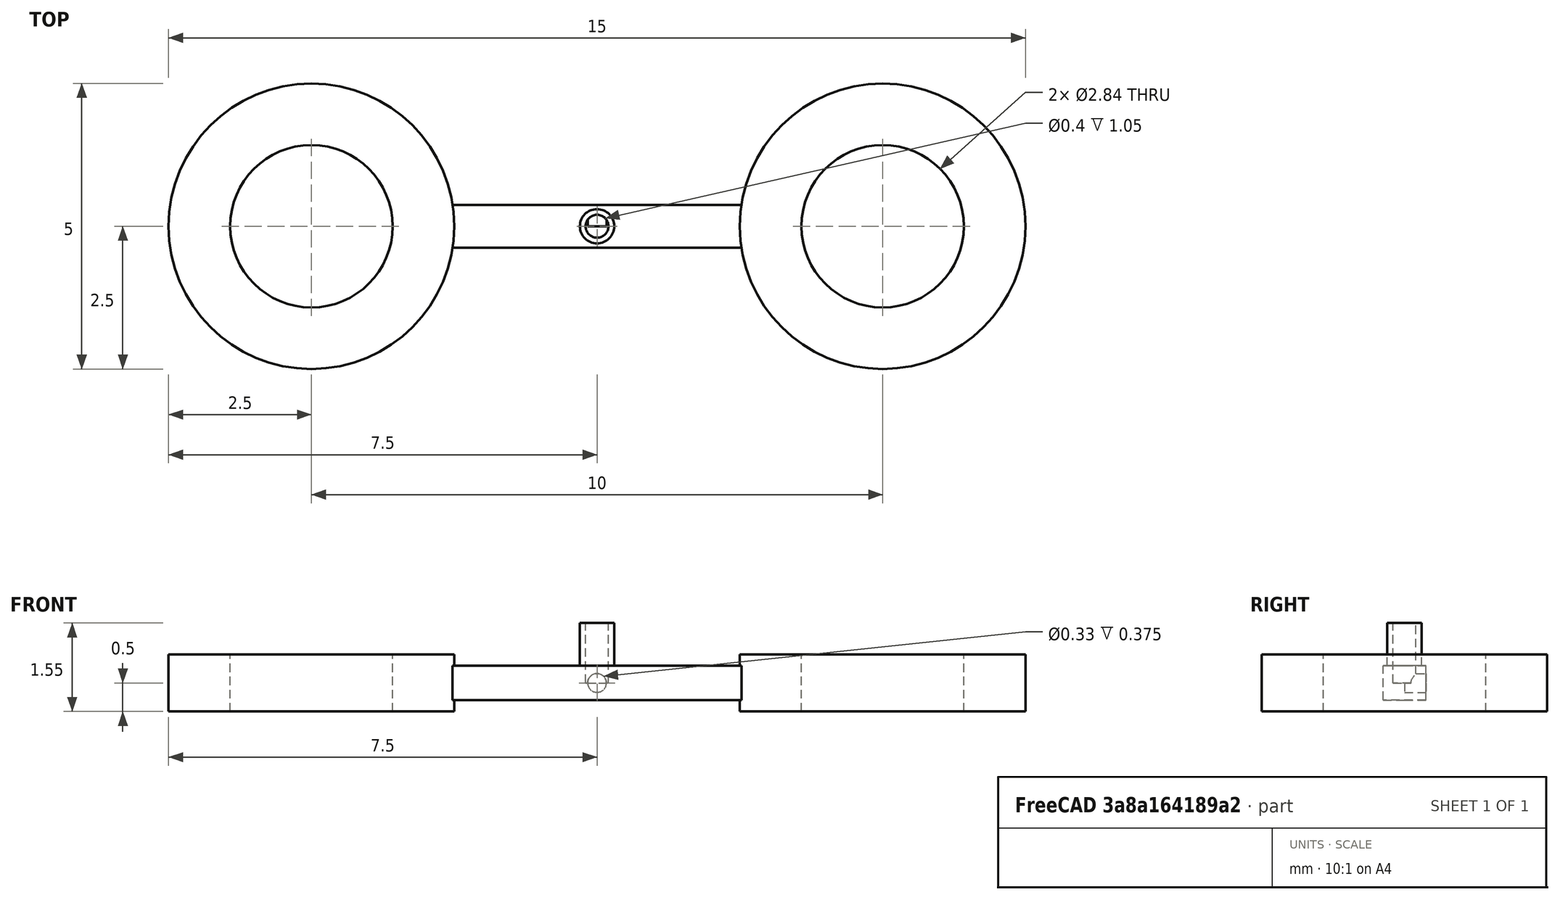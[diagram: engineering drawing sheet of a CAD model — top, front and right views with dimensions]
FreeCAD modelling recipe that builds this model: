
FCSTD DOCUMENT  (FreeCAD 0.18R15536 (Git))
Label: bowtie_3
License: All rights reserved
LicenseURL: http://en.wikipedia.org/wiki/All_rights_reserved
objects: Part::Cylinder×7, Part::MultiFuse×2, Part::Box×1, Spreadsheet::Sheet×1, Part::Cut×1
note: 11 computed .brp shape members not serialized (recipe doc carries the construction recipe); baked Part::Feature solids carry a one-line shape summary decoded from their .brp

FEATURE [Part::Cylinder] Cylinder138  label="BowTieInjectorWire"
  Angle = 360
  AttacherType = Attacher::AttachEngine3D
  Height = 8
  Placement = pos=(0,0,0) rot=(-1,0,0;1.5708rad)
  Radius = 0.165
  expr: Radius = 0.33000000000000002 / 2
FEATURE [Part::Cylinder] Cylinder136  label="BowTieNozzle"
  Angle = 360
  AttacherType = Attacher::AttachEngine3D
  Height = 9
  Radius = 0.2
FEATURE [Part::Cylinder] Cylinder  label="MountingHole1"
  Angle = 360
  AttacherType = Attacher::AttachEngine3D
  Height = 2
  Placement = pos=(-5,0,-1) rot=(0,0,1;0rad)
  Radius = 1.422
  expr: Placement.Base.x = -Sizes.STRIP_LENGTH / 2
  expr: Radius = Sizes.MOUNTING_ID / 2
FEATURE [Part::Box] Box  label="Strip"
  AttacherType = Attacher::AttachEngine3D
  Height = 0.6
  Length = 10
  Placement = pos=(-5,-0.375,-0.3) rot=(0,0,1;0rad)
  Width = 0.75
  expr: Width = Sizes.STRIP_WIDTH
  expr: Placement.Base.y = -Sizes.STRIP_WIDTH / 2
  expr: Length = Sizes.STRIP_LENGTH
  expr: Placement.Base.x = -Sizes.STRIP_LENGTH / 2
  expr: Height = Sizes.STRIP_HEIGHT
  expr: Placement.Base.z = -Sizes.STRIP_HEIGHT / 2
FEATURE [Spreadsheet::Sheet] Spreadsheet  label="Sizes"
  cells = A1=Strip height; B1(STRIP_HEIGHT)=0.59999999999999998; A2=Strip length; B2(STRIP_LENGTH)=10; A3=strip width; B3(STRIP_WIDTH)=0.75; A4=Injection width; B4(INJECTION_WIDTH)=1.5; A5=Injection length; B5(INJECTION_LENGTH)=1.5; A6=Mounting hole ID; B6(MOUNTING_ID)=2.8439999999999999; A7=Nozzle ID; B7(NOZZLE_ID)=0.33000000000000002; A8=Nozzle OD; B8(NOZZLE_OD)=0.59999999999999998; A9=Mounting hole OD; B9(MOUNTING_OD)=5; A10=Nozzle height; B10(NOZZLE_HEIGHT)=0.75; A11=Mounting hole height; B11(MOUNTING_HEIGHT)=1
FEATURE [Part::Cylinder] Cylinder139  label="MountingHole2"
  Angle = 360
  AttacherType = Attacher::AttachEngine3D
  Height = 2
  Placement = pos=(5,0,-1) rot=(0,0,1;0rad)
  Radius = 1.422
  expr: Placement.Base.x = Sizes.STRIP_LENGTH / 2
  expr: Radius = Sizes.MOUNTING_ID / 2
FEATURE [Part::Cylinder] Cylinder140  label="Nozzle_OD"
  Angle = 360
  AttacherType = Attacher::AttachEngine3D
  Height = 0.75
  Placement = pos=(0,0,0.3) rot=(0,0,1;0rad)
  Radius = 0.3
  expr: Placement.Base.z = Sizes.STRIP_HEIGHT / 2
  expr: Height = Sizes.NOZZLE_HEIGHT
  expr: Radius = Sizes.NOZZLE_OD / 2
FEATURE [Part::Cylinder] Cylinder141  label="MountingHoleOD"
  Angle = 360
  AttacherType = Attacher::AttachEngine3D
  Height = 1
  Placement = pos=(-5,0,-0.5) rot=(0,0,1;0rad)
  Radius = 2.5
  expr: Radius = Sizes.MOUNTING_OD / 2
  expr: Placement.Base.z = -Sizes.MOUNTING_HEIGHT / 2
  expr: Height = Sizes.MOUNTING_HEIGHT
  expr: Placement.Base.x = -Sizes.STRIP_LENGTH / 2
FEATURE [Part::Cylinder] Cylinder142  label="MountingHoleOD001"
  Angle = 360
  AttacherType = Attacher::AttachEngine3D
  Height = 1
  Placement = pos=(5,0,-0.5) rot=(0,0,1;0rad)
  Radius = 2.5
  expr: Placement.Base.z = -Sizes.MOUNTING_HEIGHT / 2
  expr: Height = Sizes.MOUNTING_HEIGHT
  expr: Placement.Base.x = Sizes.STRIP_LENGTH / 2
  expr: Radius = Sizes.MOUNTING_OD / 2
FEATURE [Part::MultiFuse] Fusion
  Shapes = -> [Box,Cylinder142,Cylinder141,Cylinder140]
FEATURE [Part::MultiFuse] Fusion001
  Shapes = -> [Cylinder138,Cylinder136,Cylinder,Cylinder139]
FEATURE [Part::Cut] Cut
  Base = -> Fusion
  Tool = -> Fusion001
